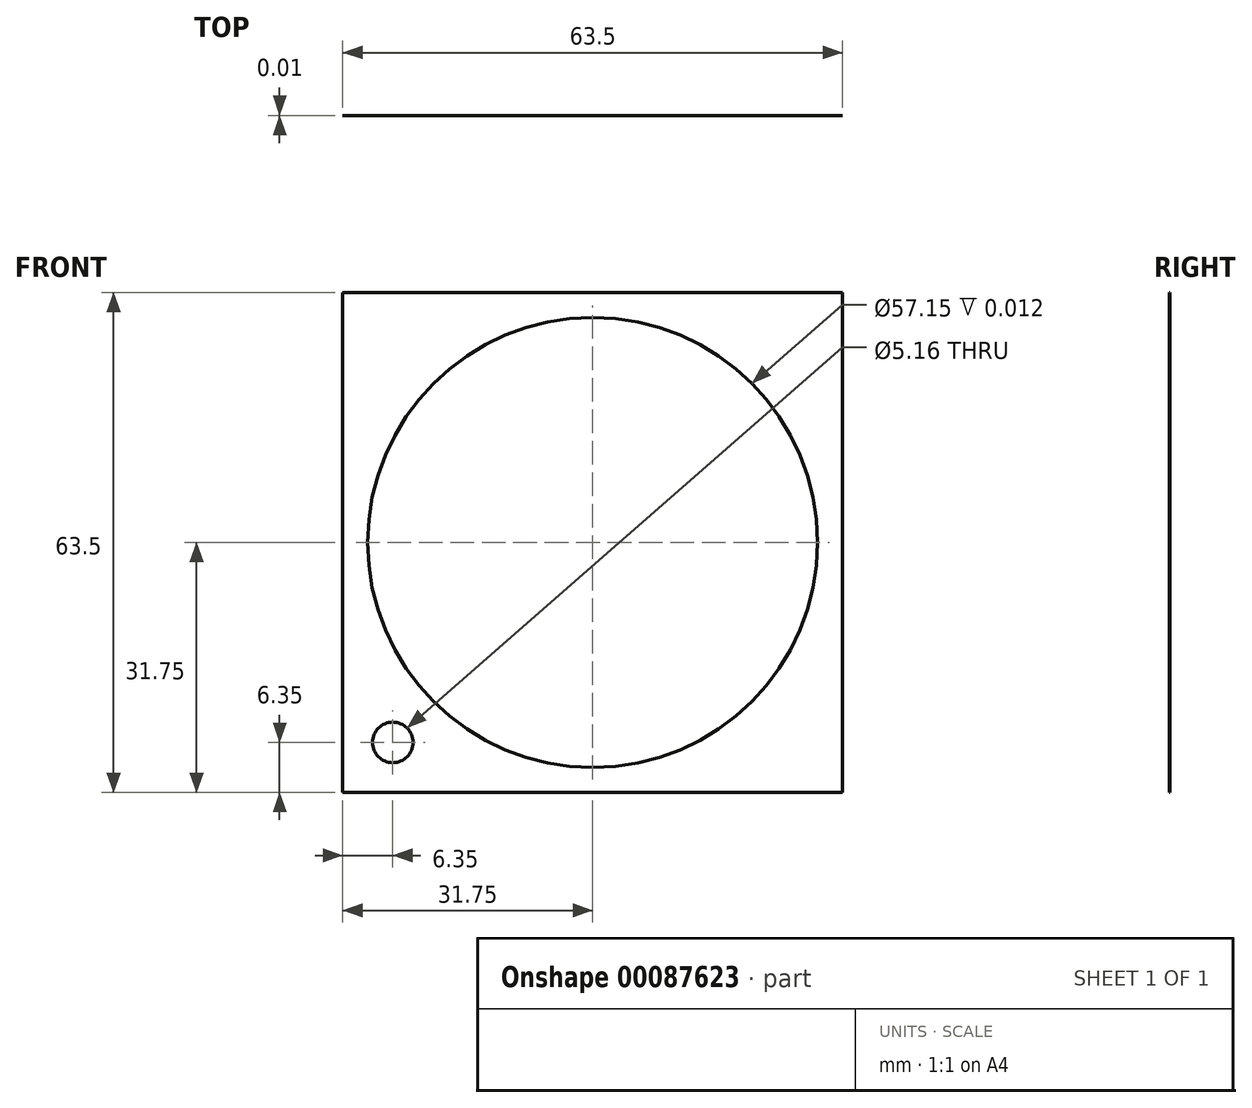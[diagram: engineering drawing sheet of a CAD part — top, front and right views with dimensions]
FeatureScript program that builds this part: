
annotation { "Feature Type Name" : "Feature", "Feature Type Description" : "" }
export const myFeature = defineFeature(function(context is Context, id is Id, definition is map)
    precondition{}
    {
        {
            var Q0;
            Q0=qCreatedBy(makeId("Front.planeOp"),FACE);
            var sketch = newSketch(context, id + "F0", { "sketchPlane" : qUnion([Q0])});
            skLineSegment(sketch, "E0.bottom", {"start": v(31.75, 31.75) * mm, "end": v(-31.75, 31.75) * mm});
            skLineSegment(sketch, "E0.top", {"start": v(31.75, -31.75) * mm, "end": v(-31.75, -31.75) * mm});
            skLineSegment(sketch, "E0.left", {"start": v(31.75, 31.75) * mm, "end": v(31.75, -31.75) * mm});
            skLineSegment(sketch, "E0.right", {"start": v(-31.75, 31.75) * mm, "end": v(-31.75, -31.75) * mm});
            skPoint(sketch, "E0.middle", {"position": v(0, 0) * mm});
            skCircle(sketch, "E1", {"center": v(0, 0) * mm, "radius": 28.58 * mm});
            skSolve(sketch);
        }
        {
            var Q0;
            Q0=makeQuery(id+"F0.imprint","IMPRINT",FACE,{"disambiguationData":[TD([[makeQuery(id+"F0.imprint","IMPRINT",EDGE,{"derivedFrom":sQuery(id+"F0.wireOp",EDGE,"E0.bottom")}),1.0]])]});
            extrude(context, id + "F1", {"entities" : qUnion([Q0]), "depth" : 5 / 406.4 * mm});
        }
        {
            var Q0;
            Q0=makeQuery(id+"F1.opExtrude","CAP_FACE",FACE,{"disambiguationData":[OSD([sQuery(id+"F0.wireOp",EDGE,"E0.bottom"),sQuery(id+"F0.wireOp",EDGE,"E0.top"),sQuery(id+"F0.wireOp",EDGE,"E0.left"),sQuery(id+"F0.wireOp",EDGE,"E0.right"),sQuery(id+"F0.wireOp",EDGE,"E1")])],"isStart":false});
            var sketch = newSketch(context, id + "F2", { "sketchPlane" : qUnion([Q0])});
            skLineSegment(sketch, "E2", {"start": v(-31.75, -31.75) * mm, "end": v(-25.4, -31.75) * mm, "construction": true});
            skLineSegment(sketch, "E3", {"start": v(-25.4, -31.75) * mm, "end": v(-25.4, -25.4) * mm});
            skCircle(sketch, "E4", {"center": v(-25.4, -25.4) * mm, "radius": 2.58 * mm});
            skSolve(sketch);
        }
        {
            var Q0;
            Q0=makeQuery(id+"F2.imprint","IMPRINT",FACE,{"disambiguationData":[TD([[makeQuery(id+"F2.imprint","IMPRINT",EDGE,{"derivedFrom":sQuery(id+"F2.wireOp",EDGE,"E4")}),1.0]])]});
            extrude(context, id + "F3", {"entities" : qUnion([Q0]), "operationType" : NewBodyOperationType.REMOVE, "oppositeDirection" : true, "depth" : 25.4 * mm});
        }
    });
